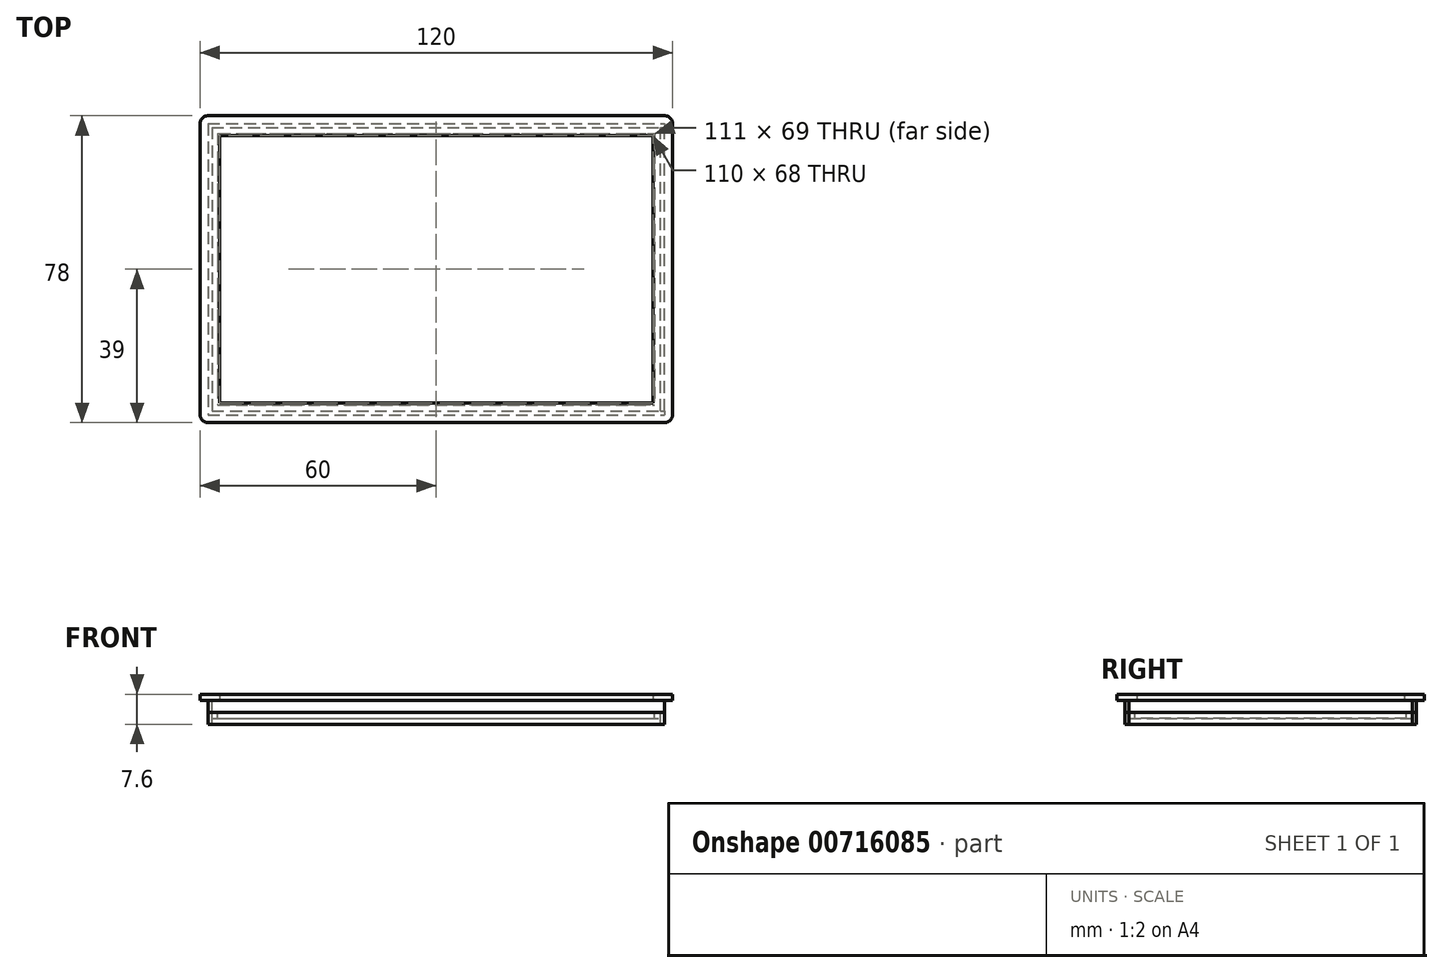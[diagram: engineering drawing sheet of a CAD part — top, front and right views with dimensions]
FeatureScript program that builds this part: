
annotation { "Feature Type Name" : "Feature", "Feature Type Description" : "" }
export const myFeature = defineFeature(function(context is Context, id is Id, definition is map)
    precondition{}
    {
        {
            var Q0;
            Q0=qCreatedBy(makeId("Top.planeOp"),FACE);
            var sketch = newSketch(context, id + "F0", { "sketchPlane" : qUnion([Q0])});
            skLineSegment(sketch, "E0.bottom", {"start": v(-58, 39) * mm, "end": v(58, 39) * mm});
            skLineSegment(sketch, "E0.top", {"start": v(-58, -39) * mm, "end": v(58, -39) * mm});
            skLineSegment(sketch, "E0.left", {"start": v(-60, 37) * mm, "end": v(-60, -37) * mm});
            skLineSegment(sketch, "E0.right", {"start": v(60, 37) * mm, "end": v(60, -37) * mm});
            skPoint(sketch, "E0.middle", {"position": v(0, 0) * mm});
            skPoint(sketch, "E1.visualSharp", {"position": v(-60, 39) * mm});
            skArc(sketch, "E1.filletArc", {"start": v(-58, 39) * mm, "mid": v(-59.41, 38.41) * mm, "end": v(-60, 37) * mm});
            skPoint(sketch, "E2.visualSharp", {"position": v(-60, -39) * mm});
            skArc(sketch, "E2.filletArc", {"start": v(-60, -37) * mm, "mid": v(-59.41, -38.41) * mm, "end": v(-58, -39) * mm});
            skPoint(sketch, "E3.visualSharp", {"position": v(60, -39) * mm});
            skArc(sketch, "E3.filletArc", {"start": v(58, -39) * mm, "mid": v(59.41, -38.41) * mm, "end": v(60, -37) * mm});
            skPoint(sketch, "E4.visualSharp", {"position": v(60, 39) * mm});
            skArc(sketch, "E4.filletArc", {"start": v(60, 37) * mm, "mid": v(59.41, 38.41) * mm, "end": v(58, 39) * mm});
            skLineSegment(sketch, "E5.bottom", {"start": v(-55, 34) * mm, "end": v(55, 34) * mm});
            skLineSegment(sketch, "E5.top", {"start": v(-55, -34) * mm, "end": v(55, -34) * mm});
            skLineSegment(sketch, "E5.left", {"start": v(-55, 34) * mm, "end": v(-55, -34) * mm});
            skLineSegment(sketch, "E5.right", {"start": v(55, 34) * mm, "end": v(55, -34) * mm});
            skLineSegment(sketch, "E6.bottom", {"start": v(-57, 36) * mm, "end": v(58, 36) * mm});
            skLineSegment(sketch, "E6.top", {"start": v(-57, -36) * mm, "end": v(58, -36) * mm});
            skLineSegment(sketch, "E6.left", {"start": v(-57, 36) * mm, "end": v(-57, -36) * mm});
            skLineSegment(sketch, "E6.right", {"start": v(57, 36) * mm, "end": v(57, -36) * mm});
            skLineSegment(sketch, "E7.bottom", {"start": v(-58, 37) * mm, "end": v(58, 37) * mm});
            skLineSegment(sketch, "E7.top", {"start": v(-58, -37) * mm, "end": v(58, -37) * mm});
            skLineSegment(sketch, "E7.left", {"start": v(-58, 37) * mm, "end": v(-58, -37) * mm});
            skLineSegment(sketch, "E7.right", {"start": v(58, 37) * mm, "end": v(58, -37) * mm});
            skSolve(sketch);
        }
        {
            var Q0;
            Q0=makeQuery(id+"F0.imprint","IMPRINT",FACE,{"disambiguationData":[TD([[makeQuery(id+"F0.imprint","IMPRINT",EDGE,{"derivedFrom":sQuery(id+"F0.wireOp",EDGE,"E0.bottom")}),-1.0]])]});
            var Q1;
            Q1=makeQuery(id+"F0.imprint","IMPRINT",FACE,{"disambiguationData":[TD([[makeQuery(id+"F0.imprint","IMPRINT",EDGE,{"derivedFrom":sQuery(id+"F0.wireOp",EDGE,"E6.bottom")}),1.0]])]});
            var Q2;
            Q2=makeQuery(id+"F0.imprint","IMPRINT",FACE,{"disambiguationData":[TD([[makeQuery(id+"F0.imprint","IMPRINT",EDGE,{"derivedFrom":sQuery(id+"F0.wireOp",EDGE,"E5.bottom")}),1.0]])]});
            var Q3;
            {var subQ3=sQuery(id+"F0.wireOp",EDGE,"E6.right");Q3=makeQuery(id+"F0.imprint","IMPRINT",FACE,{"disambiguationData":[TD([[makeQuery(id+"F0.imprint","IMPRINT",EDGE,{"derivedFrom":subQ3}),1.0]])]});}
            extrude(context, id + "F1", {"entities" : qUnion([Q0, Q1, Q2, Q3]), "depth" : 1.6 * mm, "offsetDistance" : 25 * mm});
        }
        {
            var Q0;
            {var subQ5=sQuery(id+"F0.wireOp",EDGE,"E6.left");Q0=makeQuery(id+"F0.imprint","IMPRINT",FACE,{"disambiguationData":[TD([[makeQuery(id+"F0.imprint","IMPRINT",EDGE,{"derivedFrom":subQ5}),-1.0]])]});}
            extrude(context, id + "F2", {"entities" : qUnion([Q0]), "operationType" : NewBodyOperationType.ADD, "oppositeDirection" : true, "depth" : 3 * mm, "offsetDistance" : 25 * mm});
        }
        {
            var Q0;
            Q0=makeQuery(id+"F2.opExtrude","CAP_FACE",FACE,{"disambiguationData":[OSD([sQuery(id+"F0.wireOp",EDGE,"E6.bottom"),sQuery(id+"F0.wireOp",EDGE,"E6.top"),sQuery(id+"F0.wireOp",EDGE,"E6.left"),sQuery(id+"F0.wireOp",EDGE,"E7.bottom"),sQuery(id+"F0.wireOp",EDGE,"E7.top"),sQuery(id+"F0.wireOp",EDGE,"E7.left"),sQuery(id+"F0.wireOp",EDGE,"E7.right")])],"isStart":false});
            var sketch = newSketch(context, id + "F3", { "sketchPlane" : qUnion([Q0])});
            skLineSegment(sketch, "E8.bottom", {"start": v(-55.5, -34.5) * mm, "end": v(55.5, -34.5) * mm});
            skLineSegment(sketch, "E8.top", {"start": v(-55.5, 34.5) * mm, "end": v(55.5, 34.5) * mm});
            skLineSegment(sketch, "E8.left", {"start": v(-55.5, -34.5) * mm, "end": v(-55.5, 34.5) * mm});
            skLineSegment(sketch, "E8.right", {"start": v(55.5, -34.5) * mm, "end": v(55.5, 34.5) * mm});
            skPoint(sketch, "E8.middle", {"position": v(0, 0) * mm});
            skLineSegment(sketch, "E9.bottom", {"start": v(-57, -36) * mm, "end": v(57, -36) * mm});
            skLineSegment(sketch, "E9.top", {"start": v(-57, 36) * mm, "end": v(57, 36) * mm});
            skLineSegment(sketch, "E9.left", {"start": v(-57, 36) * mm, "end": v(-57, -36) * mm});
            skLineSegment(sketch, "E9.right", {"start": v(57, 36) * mm, "end": v(57, -36) * mm});
            skLineSegment(sketch, "E10.bottom", {"start": v(57, 36) * mm, "end": v(58, 36) * mm});
            skLineSegment(sketch, "E10.top", {"start": v(57, -36) * mm, "end": v(58, -36) * mm});
            skLineSegment(sketch, "E10.right", {"start": v(58, 36) * mm, "end": v(58, -36) * mm});
            skSolve(sketch);
        }
        {
            var Q0;
            Q0=makeQuery(id+"F3.imprint","IMPRINT",FACE,{"disambiguationData":[TD([[makeQuery(id+"F3.imprint","IMPRINT",EDGE,{"derivedFrom":sQuery(id+"F3.wireOp",EDGE,"E8.bottom")}),-1.0]])]});
            extrude(context, id + "F4", {"entities" : qUnion([Q0]), "operationType" : NewBodyOperationType.ADD, "depth" : 1.5 * mm, "offsetDistance" : 25 * mm});
        }
        {
            var Q0;
            Q0=makeQuery(id+"F2.opExtrude","CAP_FACE",FACE,{"disambiguationData":[OSD([sQuery(id+"F0.wireOp",EDGE,"E6.bottom"),sQuery(id+"F0.wireOp",EDGE,"E6.top"),sQuery(id+"F0.wireOp",EDGE,"E6.left"),sQuery(id+"F0.wireOp",EDGE,"E7.bottom"),sQuery(id+"F0.wireOp",EDGE,"E7.top"),sQuery(id+"F0.wireOp",EDGE,"E7.left"),sQuery(id+"F0.wireOp",EDGE,"E7.right")])],"isStart":false});
            extrude(context, id + "F5", {"entities" : qUnion([Q0]), "depth" : 3 * mm, "offsetDistance" : 25 * mm});
        }
        {
            var Q0;
            Q0=makeQuery(id+"F3.imprint","IMPRINT",FACE,{"disambiguationData":[TD([[makeQuery(id+"F3.imprint","IMPRINT",EDGE,{"derivedFrom":sQuery(id+"F3.wireOp",EDGE,"E10.bottom")}),-1.0]])]});
            extrude(context, id + "F6", {"entities" : qUnion([Q0]), "depth" : 3 * mm, "offsetDistance" : 25 * mm});
        }
    });
